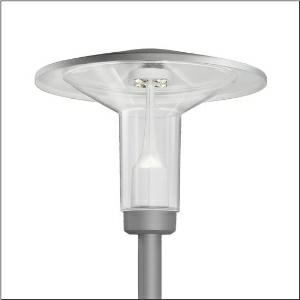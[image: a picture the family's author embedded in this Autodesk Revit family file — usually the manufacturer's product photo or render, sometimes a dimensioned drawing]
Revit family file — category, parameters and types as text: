
# Revit family: laterne_iq___st1_2a_5xa5255mf14h_e85f
name_source: partatom
category: Lighting Fixtures
units: mm (PartAtom-declared; Revit-internal decimal feet)

## family parameters
Cut with Voids When Loaded = No
Host = Face
Light Source = No
Part Type = Normal
Room Calculation Point = No
Round Connector Dimension = Use Diameter
Shared = No

## types (1)
- --- (1 x LED, 1540 lm, 11.8 W, 2700K)
    Apparent Load = 12 VA
    CIE Flux Codes = 25 63 94 98 100
    Color Rendering = 70
    Color Temperature = 2700K
    Default Elevation = 1800 mm
    Description = Lantern iQ, mast luminaire, Module 540 iQ-SR, primary light control with 3 zone facetted reflector, of plastic, silver coated, highly specular, structured, primary optical cover: cover, of PMMA, transparent, light distribution: ST1.2a, light emission: direct distribution, primary light characteristic: asymmetric, installation type: post-top, LED, High Power LED, rated luminous flux: 1.540lm, luminous efficacy: 131lm/W, light colour: 727, colour temperature: 2700K, control gear: iQ Street-Remote, control: pre-setting: logarithmic dimming characteristic, Street-Remote, Auto-Match, Temp-Guard, Lumen-Switch, Night-Set, Smart-Wire, Light-Fading, Desk-Remote (wireless, voltage-free reading and setting of iQ features in the workshop via application-optimized NFC function/RFID function), optimised constant luminous flux control (CLO 2.0), with terminal, 6-pole, max. 2.5mm², mains connection: 230..240V, AC, 50/60Hz, start of lifetime: 12W, end of service life: 12W, reduction: 6W, luminaire housing, upper part, of glass-fibre reinforced polyester, coated, Siteco® metallic grey (DB 702S), diameter: 750mm, height: 583mm, spigot size: d x l = 76 x 70mm (post-top) | with reducer (optional accessory) 60 x 70mm, mounting height: 3..5m, post-top mast mounting element, of diecast aluminium, coated, Siteco® metallic grey (DB 702S), Module 540 iQ-SR, traffic white (RAL 9016), equipment: standard, protection rating (complete): IP65, insulation class (complete): insulation class II (safety insulation), certification: CE, ENEC, VDE, packaging unit: 1 piece

Light Distribution: ST1.2a
    Height = 583 mm
    Lamp = 1 x LED
    Lamp Light Flux = 1540 lm
    Lamp Power = 11.8 W
    Lamp count = 1
    Length = 750 mm
    Luminous efficacy = 131 lm/W
    Manufacturer = Siteco
    ModVariant = No
    Model = 5XA5255MF14H
    Number of Poles = 1
    OnlyDefault = Yes
    Power Factor = 1
    Product Name = Laterne iQ | ST1.2a
    Product group = mast luminaire | pylon top
    ProductGroupID = 6100
    Protection Class = Protection class II
    Protection Degree = IP 65
    RLX_Detail_Level = 1
    RLX_Emergency_Light_Flux = 0 lm
    RLX_Emergency_Type = 0
    RLX_Emergency_Type_DB = No
    RlxData = <blob elided: 103373 chars, md5=985294a3>
    Socket = socket
    Standby Power = 0 W
    System Light Flux = 1540 lm
    System Power = 12 W
    Type Comments = factory setting: luminous flux: 100 % | dim-lin: 254 | 472 mA
    Type Image = l_1006050.jpg
    URL = http://relux.com
    VarID = @adj_152899
    Voltage = 0 V
    Weight = 0.00 kg
    Width = 0 mm  [stored 0 ft]

note: [stored X ft] marks values corroborated as IEEE doubles in the binary element streams (Revit-internal decimal feet)

## geometry (parser evidence)
native form markers: Blend x4, Sweep x10
no freeform markers — native parametric forms only
